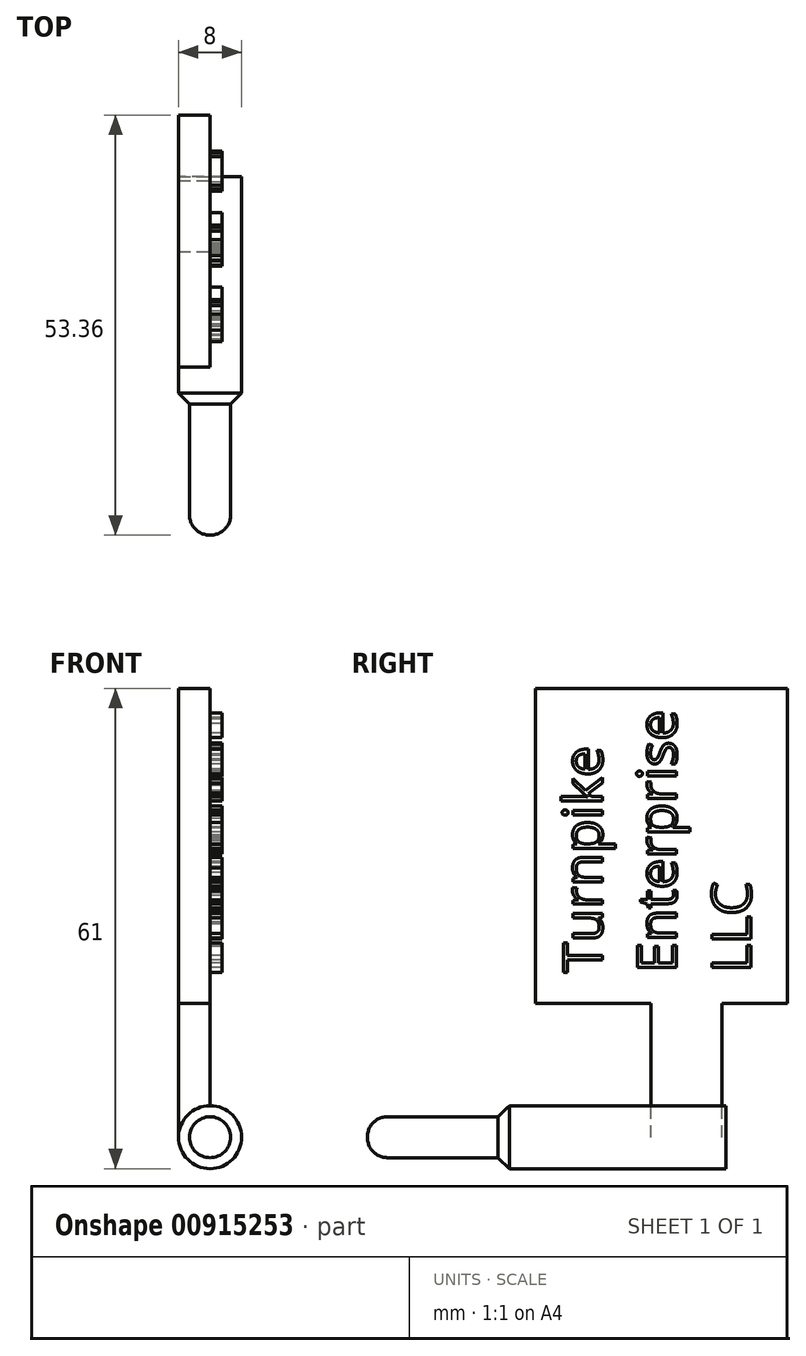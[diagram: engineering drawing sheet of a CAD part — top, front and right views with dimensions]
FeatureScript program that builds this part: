
annotation { "Feature Type Name" : "Feature", "Feature Type Description" : "" }
export const myFeature = defineFeature(function(context is Context, id is Id, definition is map)
    precondition{}
    {
        {
            var Q0;
            Q0=qCreatedBy(makeId("Right.planeOp"),FACE);
            var sketch = newSketch(context, id + "F0", { "sketchPlane" : qUnion([Q0])});
            skLineSegment(sketch, "E0.bottom", {"start": v(9, 0) * mm, "end": v(0, 0) * mm});
            skLineSegment(sketch, "E0.top", {"start": v(9, 17) * mm, "end": v(0, 17) * mm});
            skLineSegment(sketch, "E0.left", {"start": v(9, 0) * mm, "end": v(9, 17) * mm});
            skLineSegment(sketch, "E0.right", {"start": v(0, 0) * mm, "end": v(0, 17) * mm});
            skLineSegment(sketch, "E1.bottom", {"start": v(17.36, 17) * mm, "end": v(-14.64, 17) * mm});
            skLineSegment(sketch, "E1.top", {"start": v(17.36, 57) * mm, "end": v(-14.64, 57) * mm});
            skLineSegment(sketch, "E1.left", {"start": v(17.36, 17) * mm, "end": v(17.36, 57) * mm});
            skLineSegment(sketch, "E1.right", {"start": v(-14.64, 17) * mm, "end": v(-14.64, 57) * mm});
            skSolve(sketch);
        }
        {
            var Q0;
            Q0 = qSketchRegion(id + "F0", true);
            extrude(context, id + "F1", {"entities" : qUnion([Q0]), "oppositeDirection" : true, "depth" : 4 * mm, "offsetDistance" : 25 * mm});
        }
        {
            var Q0;
            Q0=qCreatedBy(makeId("Front.planeOp"),FACE);
            var sketch = newSketch(context, id + "F2", { "sketchPlane" : qUnion([Q0])});
            skCircle(sketch, "E2", {"center": v(0, 0) * mm, "radius": 2.6 * mm});
            skSolve(sketch);
        }
        {
            var Q0;
            Q0 = qSketchRegion(id + "F2", true);
            extrude(context, id + "F3", {"entities" : qUnion([Q0]), "operationType" : NewBodyOperationType.ADD, "depth" : 36 * mm, "offsetDistance" : 25 * mm});
        }
        {
            var Q0;
            Q0=qCreatedBy(makeId("Front.planeOp"),FACE);
            var sketch = newSketch(context, id + "F4", { "sketchPlane" : qUnion([Q0])});
            skCircle(sketch, "E3", {"center": v(0, 0) * mm, "radius": 4 * mm});
            skSolve(sketch);
        }
        {
            var Q0;
            Q0 = qSketchRegion(id + "F4", true);
            extrude(context, id + "F5", {"entities" : qUnion([Q0]), "operationType" : NewBodyOperationType.ADD, "endBound" : BoundingType.SYMMETRIC, "depth" : 19 * mm, "offsetDistance" : 25 * mm});
        }
        {
            var Q0;
            Q0=qCreatedBy(makeId("Front.planeOp"),FACE);
            var sketch = newSketch(context, id + "F6", { "sketchPlane" : qUnion([Q0])});
            skCircle(sketch, "E4", {"center": v(0, 0) * mm, "radius": 4 * mm});
            skSolve(sketch);
        }
        {
            var Q0;
            Q0 = qSketchRegion(id + "F6", true);
            extrude(context, id + "F7", {"entities" : qUnion([Q0]), "operationType" : NewBodyOperationType.ADD, "depth" : 20 * mm, "offsetDistance" : 25 * mm});
        }
        {
            var Q0;
            Q0=qCreatedBy(makeId("Right.planeOp"),FACE);
            var sketch = newSketch(context, id + "F8", { "sketchPlane" : qUnion([Q0])});
            skText(sketch, "E5", { "text": "Turnpike\nEnterprise\nLLC\n", "fontName": "OpenSans-Regular.ttf"});
            const initialGuessF8  = {"E5": [-0.00618, 0.0209, 0, 1, 0.005]};
            skSetInitialGuess(sketch, initialGuessF8);
            skSolve(sketch);
        }
        {
            var Q0;
            Q0 = qSketchRegion(id + "F8", true);
            extrude(context, id + "F9", {"entities" : qUnion([Q0]), "operationType" : NewBodyOperationType.ADD, "depth" : 1.5 * mm, "offsetDistance" : 25 * mm});
        }
        {
            var Q0;
            Q0=makeQuery(id+"F7.opExtrude","CAP_EDGE",EDGE,{"disambiguationData":[OSD([sQuery(id+"F6.wireOp",EDGE,"E4")])],"isStart":false});
            chamfer(context, id + "F10", {"entities" : qUnion([Q0]), "width" : 2 * mm, "tangentPropagation" : true});
        }
        {
            var Q0;
            Q0=makeQuery(id+"F3.opExtrude","CAP_EDGE",EDGE,{"disambiguationData":[OSD([sQuery(id+"F2.wireOp",EDGE,"E2")])],"isStart":false});
            fillet(context, id + "F11", {"entities" : qUnion([Q0]), "radius" : 2.5 * mm, "tangentPropagation" : true, "allowEdgeOverflow" : false});
        }
    });
